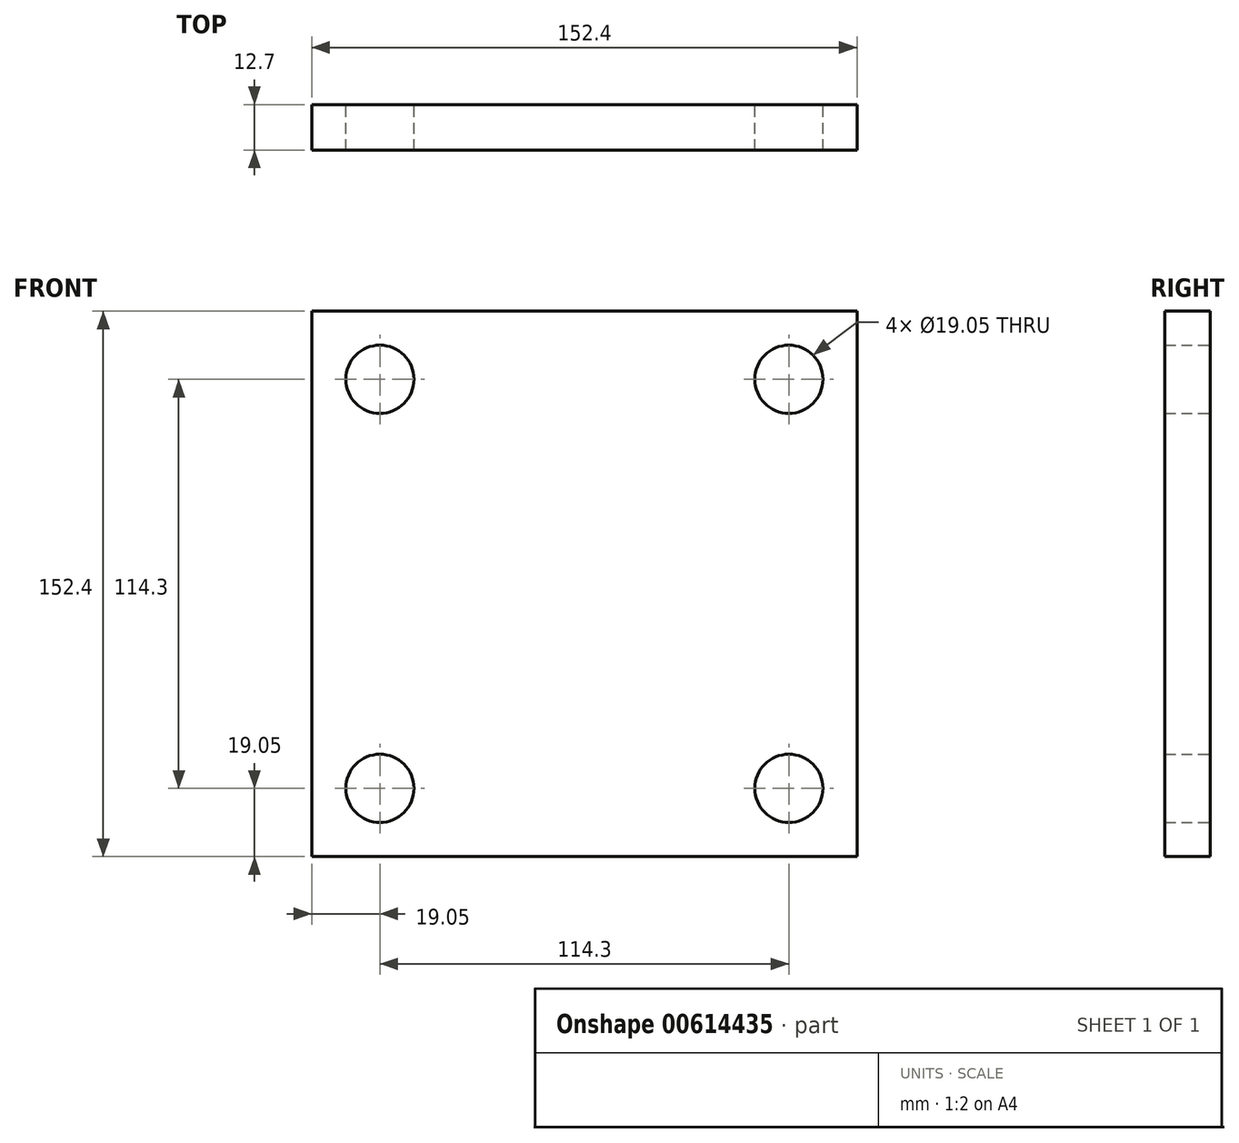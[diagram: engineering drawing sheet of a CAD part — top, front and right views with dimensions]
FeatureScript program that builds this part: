
annotation { "Feature Type Name" : "Feature", "Feature Type Description" : "" }
export const myFeature = defineFeature(function(context is Context, id is Id, definition is map)
    precondition{}
    {
        {
            var Q0;
            Q0=qCreatedBy(makeId("Front.planeOp"),FACE);
            var sketch = newSketch(context, id + "F0", { "sketchPlane" : qUnion([Q0])});
            skLineSegment(sketch, "E0.bottom", {"start": v(76.2, 76.2) * mm, "end": v(-76.2, 76.2) * mm});
            skLineSegment(sketch, "E0.top", {"start": v(76.2, -76.2) * mm, "end": v(-76.2, -76.2) * mm});
            skLineSegment(sketch, "E0.left", {"start": v(76.2, 76.2) * mm, "end": v(76.2, -76.2) * mm});
            skLineSegment(sketch, "E0.right", {"start": v(-76.2, 76.2) * mm, "end": v(-76.2, -76.2) * mm});
            skPoint(sketch, "E0.middle", {"position": v(0, 0) * mm});
            skCircle(sketch, "E1", {"center": v(57.15, 57.15) * mm, "radius": 9.53 * mm});
            skCircle(sketch, "E2", {"center": v(57.15, -57.15) * mm, "radius": 9.53 * mm});
            skCircle(sketch, "E3", {"center": v(-57.15, -57.15) * mm, "radius": 9.53 * mm});
            skCircle(sketch, "E4", {"center": v(-57.15, 57.15) * mm, "radius": 9.53 * mm});
            skSolve(sketch);
        }
        {
            var Q0;
            Q0=makeQuery(id+"F0.imprint","IMPRINT",FACE,{"disambiguationData":[TD([[makeQuery(id+"F0.imprint","IMPRINT",EDGE,{"derivedFrom":sQuery(id+"F0.wireOp",EDGE,"E0.bottom")}),1.0]])]});
            extrude(context, id + "F1", {"entities" : qUnion([Q0]), "depth" : 12.7 * mm, "offsetDistance" : 25.4 * mm});
        }
    });
